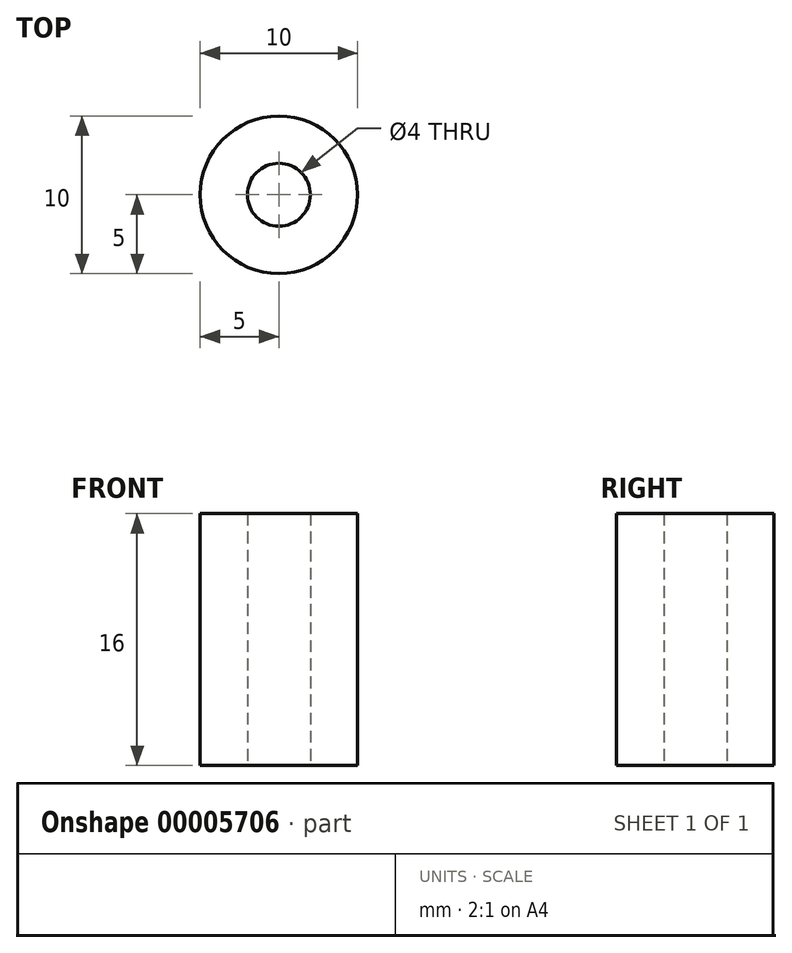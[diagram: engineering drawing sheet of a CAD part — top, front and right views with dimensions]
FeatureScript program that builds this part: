
annotation { "Feature Type Name" : "Feature", "Feature Type Description" : "" }
export const myFeature = defineFeature(function(context is Context, id is Id, definition is map)
    precondition{}
    {
        {
            var Q0;
            Q0=qCreatedBy(makeId("Top.planeOp"),FACE);
            var sketch = newSketch(context, id + "F0", { "sketchPlane" : qUnion([Q0])});
            skCircle(sketch, "E0", {"center": v(0, 0) * mm, "radius": 2 * mm});
            skCircle(sketch, "E1", {"center": v(0, 0) * mm, "radius": 5 * mm});
            skSolve(sketch);
        }
        {
            var Q0;
            Q0=makeQuery(id+"F0.imprint","IMPRINT",FACE,{"disambiguationData":[TD([[makeQuery(id+"F0.imprint","IMPRINT",EDGE,{"derivedFrom":sQuery(id+"F0.wireOp",EDGE,"E0")}),-1.0]])]});
            extrude(context, id + "F1", {"entities" : qUnion([Q0]), "depth" : 16 * mm});
        }
    });
